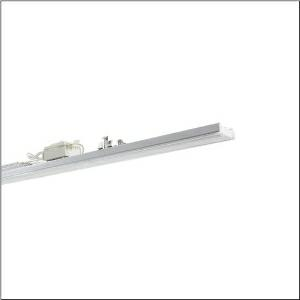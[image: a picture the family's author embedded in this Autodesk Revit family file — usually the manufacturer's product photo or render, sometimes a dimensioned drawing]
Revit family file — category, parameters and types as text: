
# Revit family: licross_11_recessed_tw_51tl12tnt9xx
name_source: partatom
category: Lighting Fixtures
units: mm (PartAtom-declared; Revit-internal decimal feet)

## family parameters
Cut with Voids When Loaded = No
Host = Face
Light Source = No
Part Type = Normal
Room Calculation Point = No
Round Connector Dimension = Use Diameter
Shared = No

## types (1)
- --- (1 x LED 2700 K ... 6500 K, 9050 lm, 56 W, 2700K)
    Apparent Load = 56 VA
    CIE Flux Codes = 66 91 98 100 100
    Color Rendering = 80
    Color Temperature = 2700K
    Default Elevation = 1800 mm
    Description = Licross 11 Recessed TW, luminaire insert, of sheet steel, galvanised, coil coated, white, length: 1.500mm, width: 66mm, height: 67mm, LED rated luminous flux: 9.050lm, light colour: 8tw, SDCM (Standard Deviation of Colour Matching)MacAdam ≤ 2 SDCM (initial), control gear: DALI DT8, with plug, 5-pole, with phase selection, mains connection: 220..240V, AC, 50/60Hz, rated input power: 56W, internal wiring halogen-free, primary optical cover: cover, of PMMA, light emission: direct distribution, primary light characteristic: symmetric, protection rating (complete): IP40, insulation class (complete): insulation class I (protective earthing), certification: CE, ENEC, VDE, UKCA, protection symbol: D if used in an environment without relevant dust loads with corresponding accessories, impact resistance: IK06, permissible ambient temperature for indoor applications: -25..+35°C, corresponds to IFS (International Featured Standards) requirements for safety and quality in the food industry, reducing of maximum allowable ambient temperature of 5°C with ceiling mounting, LABS conformity tested according to VDMA 24364:2018-05, The light source and the operating device comply with the requirements of the Ecodesign Regulation (EU) 2019/2020 and are replaceable in accordance with this regulation, packaging unit: 1 piece
    Height = 58 mm
    Lamp = 1 x LED 2700 K ... 6500 K
    Lamp Light Flux = 9050 lm
    Lamp Power = 56 W
    Lamp count = 1
    Length = 1500 mm
    Luminous efficacy = 162 lm/W
    Manufacturer = Siteco
    ModVariant = No
    Model = 51TL12TNT9XX
    Mounting Place = Ceiling
    Mounting Type = Pendant
    Number of Poles = 1
    OnlyDefault = Yes
    Power Factor = 1
    Product Name = Licross 11 Recessed TW
    Product group = luminaire insert | ceiling pendant
    ProductGroupID = 901
    Protection Class = Protection class I
    Protection Degree = IP 40
    RLX_Detail_Level = 1
    RLX_Emergency_Light_Flux = 0 lm
    RLX_Emergency_Type = 0
    RLX_Emergency_Type_DB = No
    RlxData = <blob elided: 21097 chars, md5=79a82fef>
    Socket = socket
    Standby Power = 0 W
    System Light Flux = 9050 lm
    System Power = 56 W
    Type Comments = individual setting: CCT=2700K
    Type Image = l_1296930.jpg
    URL = http://relux.com
    VarID = @adj_055971
    Voltage = 0 V
    Weight = 0.00 kg
    Width = 66 mm

## geometry (parser evidence)
native form markers: Blend x4, Sweep x11
no freeform markers — native parametric forms only
